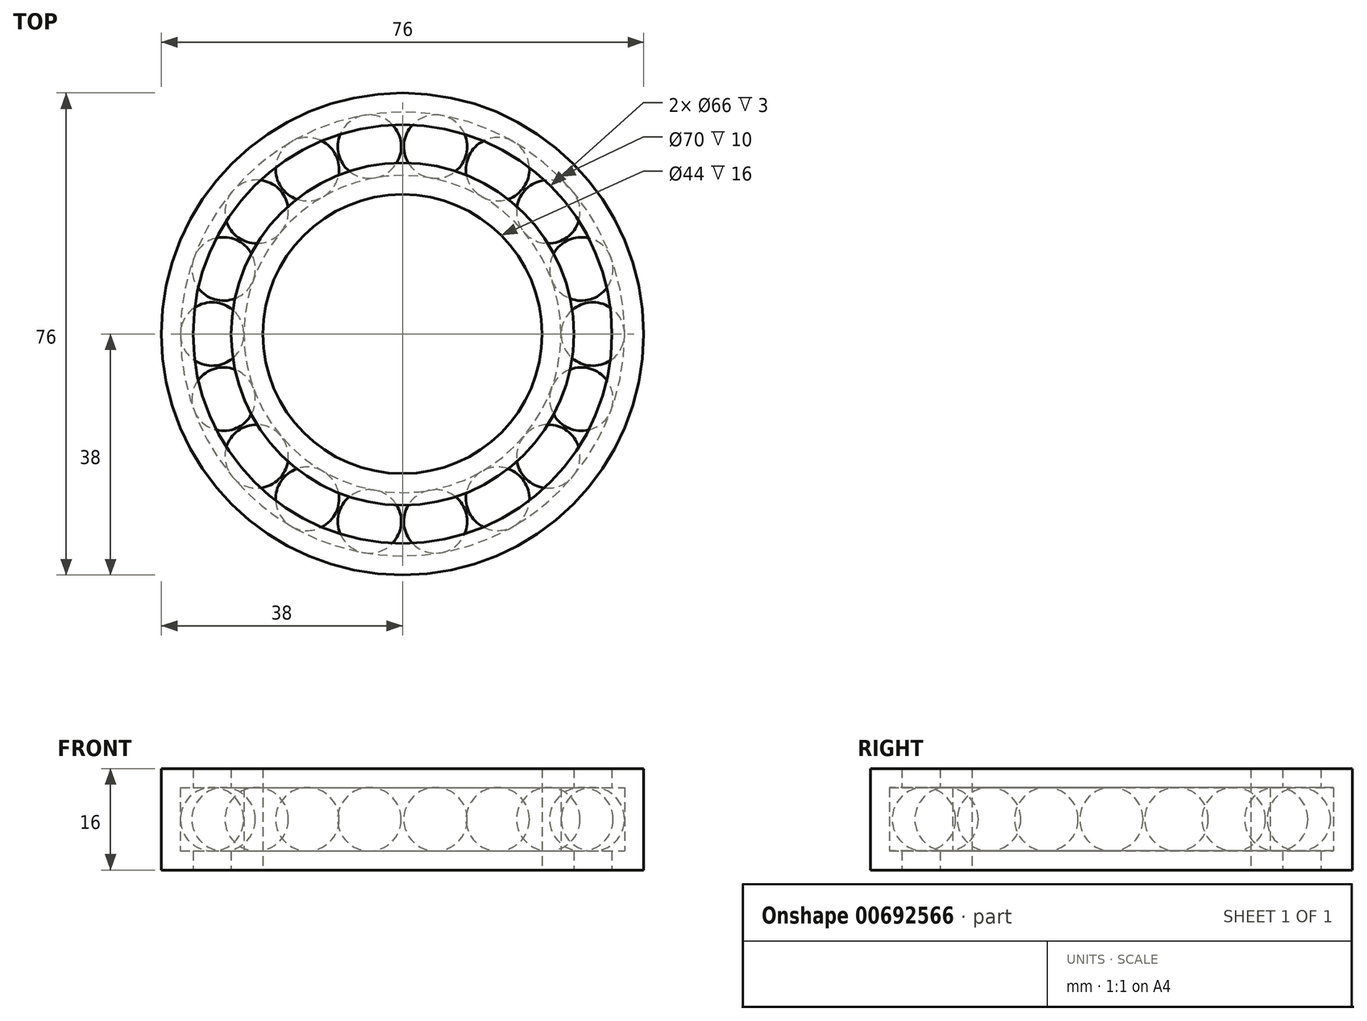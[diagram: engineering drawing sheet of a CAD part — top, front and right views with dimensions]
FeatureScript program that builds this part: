
annotation { "Feature Type Name" : "Feature", "Feature Type Description" : "" }
export const myFeature = defineFeature(function(context is Context, id is Id, definition is map)
    precondition{}
    {
        {
            var Q0;
            Q0=qCreatedBy(makeId("Front.planeOp"),FACE);
            var sketch = newSketch(context, id + "F0", { "sketchPlane" : qUnion([Q0])});
            skArc(sketch, "E0", {"start": v(-35, 0) * mm, "mid": v(-30, -5) * mm, "end": v(-25, 0) * mm});
            skLineSegment(sketch, "E1", {"start": v(-35, 0) * mm, "end": v(-25, 0) * mm});
            skSolve(sketch);
        }
        {
            var Q0;
            Q0=makeQuery(id+"F0.imprint","IMPRINT",FACE,{"disambiguationData":[TD([[makeQuery(id+"F0.imprint","IMPRINT",EDGE,{"derivedFrom":sQuery(id+"F0.wireOp",EDGE,"E0")}),1.0]])]});
            var Q1;
            Q1=sQuery(id+"F0.wireOp",EDGE,"E1");
            revolve(context, id + "F1", {"entities" : qUnion([Q0]), "axis" : qUnion([Q1]), "revolveType" : RevolveType.FULL});
        }
        {
            var Q0;
            Q0=qCreatedBy(makeId("Top.planeOp"),FACE);
            var sketch = newSketch(context, id + "F2", { "sketchPlane" : qUnion([Q0])});
            skCircle(sketch, "E2", {"center": v(0, 0) * mm, "radius": 30 * mm, "construction": true});
            skSolve(sketch);
        }
        {
            var Q0;
            Q0=makeQuery(id+"F1.opRevolve","SWEPT_BODY",BODY,{"disambiguationData":[OSD([sQuery(id+"F0.wireOp",EDGE,"E0"),sQuery(id+"F0.wireOp",EDGE,"E1")])]});
            var Q1;
            Q1=sQuery(id+"F2.wireOp",EDGE,"E2");
            circularPattern(context, id + "F3", {"entities" : qUnion([Q0]), "axis" : qUnion([Q1]), "angle" : 360 * degree, "instanceCount" : 18, "equalSpace" : true});
        }
        {
            var Q0;
            Q0=qCreatedBy(makeId("Front.planeOp"),FACE);
            var sketch = newSketch(context, id + "F4", { "sketchPlane" : qUnion([Q0])});
            skLineSegment(sketch, "E3.bottom", {"start": v(-35, 5) * mm, "end": v(-33, 5) * mm});
            skLineSegment(sketch, "E3.top", {"start": v(-35, -5) * mm, "end": v(-33, -5) * mm});
            skLineSegment(sketch, "E3.left", {"start": v(-35, 5) * mm, "end": v(-35, -5) * mm});
            skLineSegment(sketch, "E3.right", {"start": v(-25, 5) * mm, "end": v(-25, -5) * mm});
            skPoint(sketch, "E3.middle", {"position": v(-30, 0) * mm});
            skLineSegment(sketch, "E4.bottom", {"start": v(-38, 8) * mm, "end": v(-33, 8) * mm});
            skLineSegment(sketch, "E4.top", {"start": v(-38, -8) * mm, "end": v(-33, -8) * mm});
            skLineSegment(sketch, "E4.left", {"start": v(-38, 8) * mm, "end": v(-38, -8) * mm});
            skLineSegment(sketch, "E4.right", {"start": v(-22, 8) * mm, "end": v(-22, -8) * mm});
            skLineSegment(sketch, "E5", {"start": v(-33, 8) * mm, "end": v(-33, 5) * mm});
            skLineSegment(sketch, "E6", {"start": v(-33, -5) * mm, "end": v(-33, -8) * mm});
            skLineSegment(sketch, "E7", {"start": v(-27, 8) * mm, "end": v(-27, 5) * mm});
            skPoint(sketch, "E7.endSnap0", {"position": v(-30, 5) * mm});
            skLineSegment(sketch, "E8", {"start": v(-27, -5) * mm, "end": v(-27, -8) * mm});
            skLineSegment(sketch, "E9.trimOffspring", {"start": v(-27, 8) * mm, "end": v(-22, 8) * mm});
            skLineSegment(sketch, "E10.trimOffspring", {"start": v(-27, 5) * mm, "end": v(-25, 5) * mm});
            skLineSegment(sketch, "E11.trimOffspring", {"start": v(-27, -5) * mm, "end": v(-25, -5) * mm});
            skLineSegment(sketch, "E12.trimOffspring", {"start": v(-27, -8) * mm, "end": v(-22, -8) * mm});
            skSolve(sketch);
        }
        {
            var Q0;
            Q0=makeQuery(id+"F4.imprint","IMPRINT",FACE,{"disambiguationData":[TD([[makeQuery(id+"F4.imprint","IMPRINT",EDGE,{"derivedFrom":sQuery(id+"F4.wireOp",EDGE,"E3.right")}),1.0]])]});
            var Q1;
            Q1=makeQuery(id+"F4.imprint","IMPRINT",FACE,{"disambiguationData":[TD([[makeQuery(id+"F4.imprint","IMPRINT",EDGE,{"derivedFrom":sQuery(id+"F4.wireOp",EDGE,"E3.bottom")}),1.0]])]});
            var Q2;
            Q2=sQuery(id+"F2.wireOp",EDGE,"E2");
            revolve(context, id + "F5", {"entities" : qUnion([Q0, Q1]), "axis" : qUnion([Q2]), "revolveType" : RevolveType.FULL});
        }
    });
